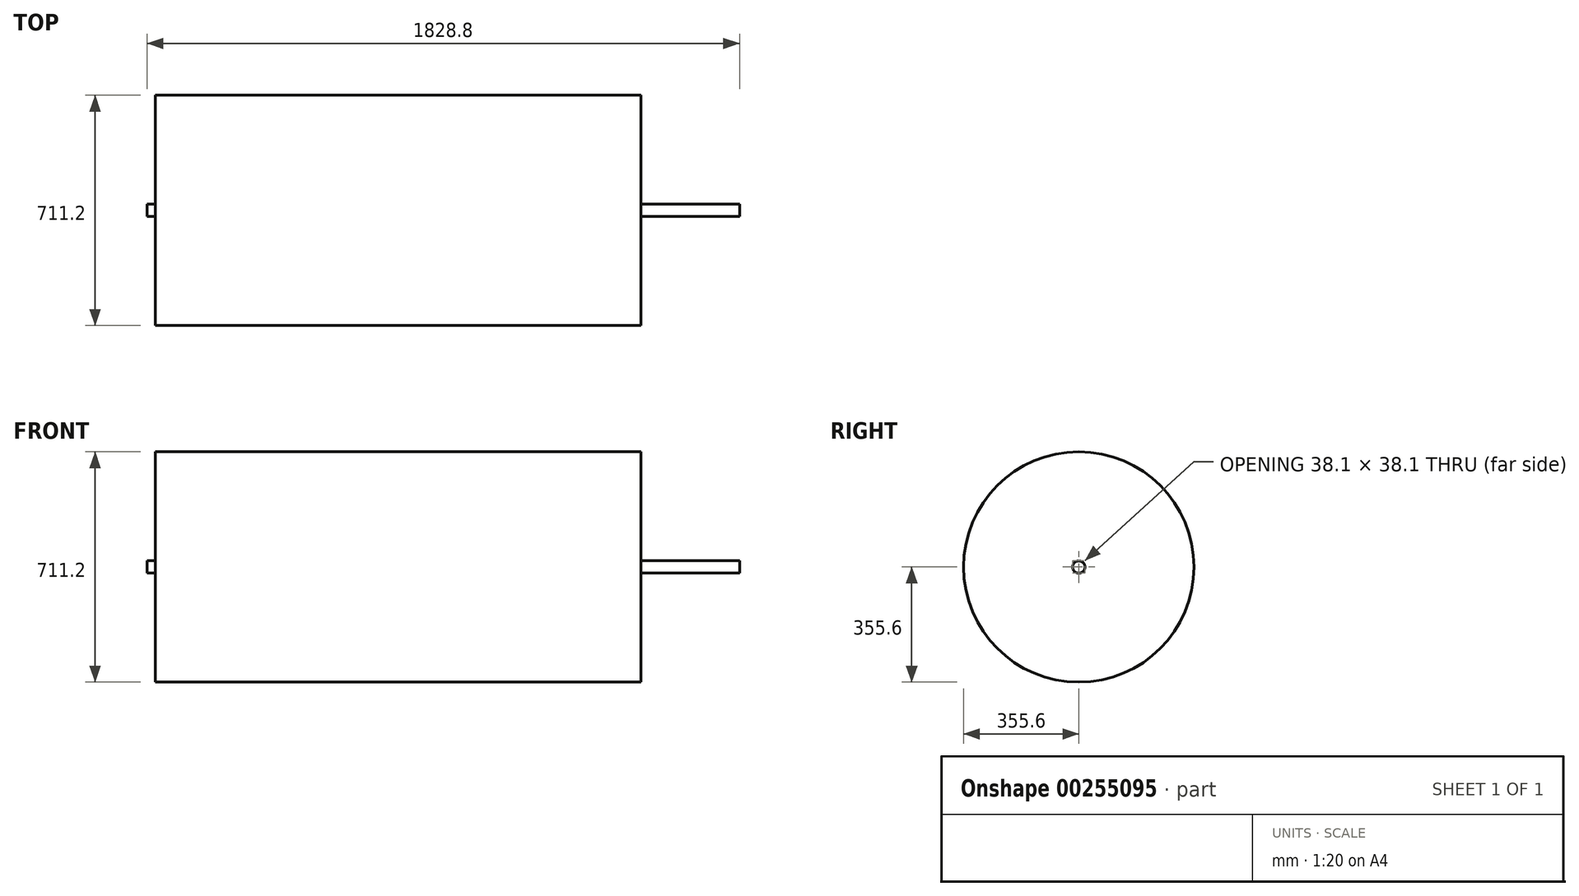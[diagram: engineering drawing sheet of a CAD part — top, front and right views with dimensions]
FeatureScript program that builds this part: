
annotation { "Feature Type Name" : "Feature", "Feature Type Description" : "" }
export const myFeature = defineFeature(function(context is Context, id is Id, definition is map)
    precondition{}
    {
        {
            var Q0;
            Q0=qCreatedBy(makeId("Right.planeOp"),FACE);
            var sketch = newSketch(context, id + "F0", { "sketchPlane" : qUnion([Q0])});
            skCircle(sketch, "E0", {"center": v(0, 0) * mm, "radius": 19.05 * mm});
            skSolve(sketch);
        }
        {
            var Q0;
            Q0 = qSketchRegion(id + "F0", true);
            extrude(context, id + "F1", {"entities" : qUnion([Q0]), "oppositeDirection" : true, "depth" : 1828.8 * mm});
        }
        {
            var Q0;
            Q0=makeQuery(id+"F1.opExtrude","CAP_FACE",FACE,{"disambiguationData":[OSD([sQuery(id+"F0.wireOp",EDGE,"E0")])],"isStart":false});
            var sketch = newSketch(context, id + "F2", { "sketchPlane" : qUnion([Q0])});
            skCircle(sketch, "E1", {"center": v(0, 0) * mm, "radius": 355.6 * mm});
            skSolve(sketch);
        }
        {
            var Q0;
            Q0 = qSketchRegion(id + "F2", true);
            extrude(context, id + "F3", {"entities" : qUnion([Q0]), "operationType" : NewBodyOperationType.ADD, "oppositeDirection" : true, "depth" : 1524 * mm, "hasSecondDirection" : true, "secondDirectionOppositeDirection" : true, "secondDirectionDepth" : 25.4 * mm});
        }
    });
